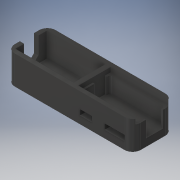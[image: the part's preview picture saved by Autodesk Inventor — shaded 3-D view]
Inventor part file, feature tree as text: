
AUTODESK INVENTOR PART (.ipt)
format: ipt  version: 2019 (Build 230136000, 136)  size: 226,816 bytes
history: native  units: in
note: dims shown in document units (in); Inventor stores cm internally (conversion verified against a paired STEP export)
features: extrude x5, sketch x5, fillet x2, chamfer x1
ambient origin geometry x8: Origin, YZ Plane, XZ Plane, XY Plane, X Axis, Y Axis, Z Axis, Center Point
bodies: Body1 (feature_tree)
feature tree (13):
  extrude  "Extrusion2"  Depth=1.9685in
  extrude  "Extrusion3"  Depth=2.8346in
  extrude  "Extrusion5"  Depth=1.0236in TaperAngle=0.0deg
  fillet  "Fillet2"  Radius=2.6772in
  extrude  "Extrusion7"  Depth=0.8in
  extrude  "Extrusion8"  Depth=0.1181in
  fillet  "Fillet3"  Radius=0.5906in
  chamfer  "Chamfer1"  Distance=0.2756in
  sketch  "Sketch2"  dims[d4=6.1024in d5=1.9685in]
  sketch  "Sketch4"  dims[d6=1.378in d7=0.0in d8=2.8346in]
  sketch  "Sketch5"  dims[d9=1.5748in d10=1.0236in d11=0.0in d12=2.6772in]
  sketch  "Sketch7"  dims[d13=1.3386in d17=0.8in]
  sketch  "Sketch9"  dims[d18=0.7874in d19=0.0in d20=0.1181in d29=0.5906in d30=0.2756in d32=0.0in d33=0.25in d34=0.0in d35=0.4882in d36=0.4724in d37=0.2756in d38=0.4724in d39=0.2756in d40=1.6299in d41=2.126in d43=0.5906in d44=0.1575in d45=2.8346in d46=1.5354in d47=0.1969in d48=1.1811in d49=0.0in d50=0.7in d51=0.3937in d52=0.315in d53=0.35in d54=0.125in d55=45.0deg]
